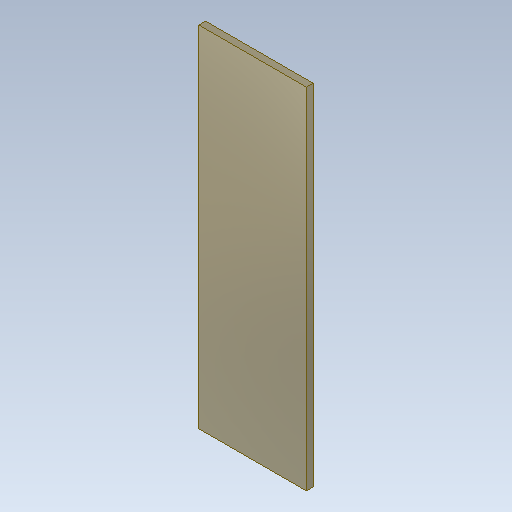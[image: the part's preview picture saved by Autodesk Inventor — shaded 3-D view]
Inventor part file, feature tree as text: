
AUTODESK INVENTOR PART (.ipt)
format: ipt  version: 2020.1 (Build 241239000, 239)  size: 98,816 bytes
history: native  units: mm
features: extrude x1, sketch x1
ambient origin geometry x8: Origin, YZ Plane, XZ Plane, XY Plane, X Axis, Y Axis, Z Axis, Center Point
bodies: Solid1 (feature_tree)
feature tree (2):
  extrude  "Extrusion1"  Depth=9.165mm
  sketch  "Sketch1"  dims[d0=18.33mm d1=9.165mm d2=26.0mm d3=8.0mm d4=0.5mm d5=0.0mm]
